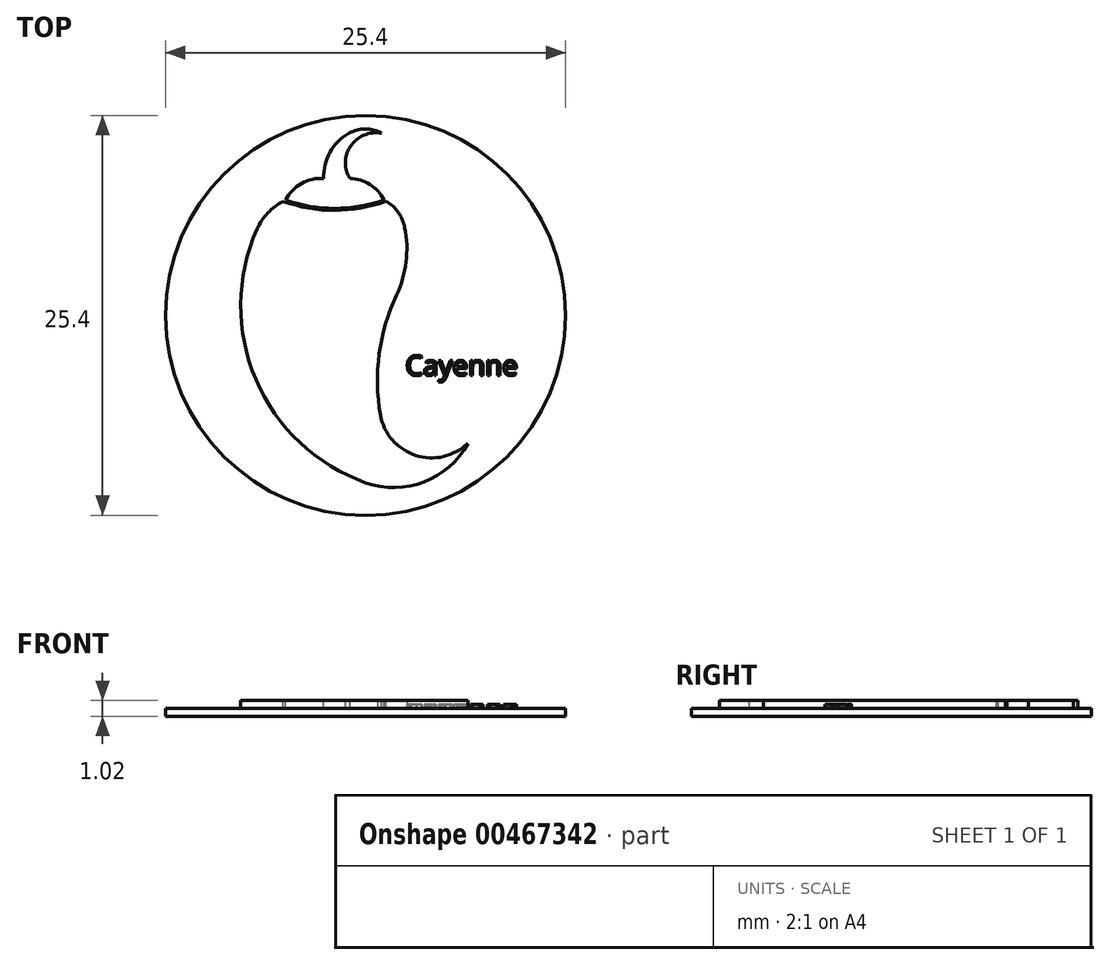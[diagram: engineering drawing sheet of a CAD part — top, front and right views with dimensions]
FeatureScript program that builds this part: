
annotation { "Feature Type Name" : "Feature", "Feature Type Description" : "" }
export const myFeature = defineFeature(function(context is Context, id is Id, definition is map)
    precondition{}
    {
        {
            var Q0;
            Q0=qCreatedBy(makeId("Top.planeOp"),FACE);
            var sketch = newSketch(context, id + "F0", { "sketchPlane" : qUnion([Q0])});
            skCircle(sketch, "E0", {"center": v(0, 0) * mm, "radius": 12.7 * mm});
            skSolve(sketch);
        }
        {
            var Q0;
            Q0 = qSketchRegion(id + "F0", true);
            extrude(context, id + "F1", {"entities" : qUnion([Q0]), "depth" : 0.5 * mm});
        }
        {
            var Q0;
            Q0=makeQuery(id+"F1.opExtrude","CAP_FACE",FACE,{"disambiguationData":[OSD([sQuery(id+"F0.wireOp",EDGE,"E0")])],"isStart":false});
            var sketch = newSketch(context, id + "F2", { "sketchPlane" : qUnion([Q0])});
            skArc(sketch, "E1", {"start": v(0, -10.63) * mm, "mid": v(3.71, -10.58) * mm, "end": v(6.5, -8.12) * mm});
            skArc(sketch, "E2", {"start": v(-6.9, 5.47) * mm, "mid": v(-6.96, -4.08) * mm, "end": v(0, -10.63) * mm});
            skArc(sketch, "E3", {"start": v(-4.06, 7.62) * mm, "mid": v(-5.75, 6.91) * mm, "end": v(-6.9, 5.47) * mm});
            skLineSegment(sketch, "E4", {"start": v(-4.06, 7.62) * mm, "end": v(0, 7.62) * mm});
            skArc(sketch, "E5", {"start": v(2.5, 5.58) * mm, "mid": v(1.6, 7.04) * mm, "end": v(0, 7.62) * mm});
            skArc(sketch, "E6", {"start": v(1.97, 1.3) * mm, "mid": v(2.57, 3.4) * mm, "end": v(2.5, 5.58) * mm});
            skArc(sketch, "E7", {"start": v(1.97, 1.3) * mm, "mid": v(0.87, -2.43) * mm, "end": v(0.95, -6.32) * mm});
            skArc(sketch, "E8", {"start": v(0.95, -6.32) * mm, "mid": v(3.18, -8.9) * mm, "end": v(6.5, -8.12) * mm});
            skSolve(sketch);
        }
        {
            var Q0;
            Q0 = qSketchRegion(id + "F2", true);
            extrude(context, id + "F3", {"entities" : qUnion([Q0]), "operationType" : NewBodyOperationType.ADD, "depth" : 0.5 * mm});
        }
        {
            var Q0;
            Q0=makeQuery(id+"F3.opExtrude","CAP_FACE",FACE,{"disambiguationData":[OSD([sQuery(id+"F2.wireOp",EDGE,"E1"),sQuery(id+"F2.wireOp",EDGE,"E2"),sQuery(id+"F2.wireOp",EDGE,"E3"),sQuery(id+"F2.wireOp",EDGE,"E4"),sQuery(id+"F2.wireOp",EDGE,"E5"),sQuery(id+"F2.wireOp",EDGE,"E6"),sQuery(id+"F2.wireOp",EDGE,"E7"),sQuery(id+"F2.wireOp",EDGE,"E8")])],"isStart":false});
            var sketch = newSketch(context, id + "F4", { "sketchPlane" : qUnion([Q0])});
            skArc(sketch, "E9", {"start": v(-2.65, 8.69) * mm, "mid": v(-4.07, 8.39) * mm, "end": v(-5.07, 7.32) * mm});
            skArc(sketch, "E10", {"start": v(-1.04, 11.57) * mm, "mid": v(-2.26, 10.36) * mm, "end": v(-2.65, 8.69) * mm});
            skArc(sketch, "E11", {"start": v(1.03, 11.57) * mm, "mid": v(0, 11.84) * mm, "end": v(-1.04, 11.57) * mm});
            skArc(sketch, "E12", {"start": v(1.03, 11.57) * mm, "mid": v(-0.1, 11.45) * mm, "end": v(-0.98, 10.7) * mm});
            skArc(sketch, "E13", {"start": v(-0.98, 10.7) * mm, "mid": v(-1.28, 9.7) * mm, "end": v(-0.98, 8.69) * mm});
            skArc(sketch, "E14", {"start": v(1.16, 7.34) * mm, "mid": v(0.28, 8.32) * mm, "end": v(-0.98, 8.69) * mm});
            skArc(sketch, "E15", {"start": v(-5.07, 7.32) * mm, "mid": v(-1.95, 7.04) * mm, "end": v(1.16, 7.34) * mm});
            skSolve(sketch);
        }
        {
            var Q0;
            Q0 = qSketchRegion(id + "F4", true);
            extrude(context, id + "F5", {"entities" : qUnion([Q0]), "operationType" : NewBodyOperationType.ADD, "oppositeDirection" : true, "depth" : 0.5 * mm});
        }
        {
            var Q0;
            Q0=makeQuery(id+"F5.boolean.opBoolean","MERGE",FACE,{"derivedFrom":[makeQuery(id+"F3.opExtrude","CAP_FACE",FACE,{"disambiguationData":[OSD([sQuery(id+"F2.wireOp",EDGE,"E1"),sQuery(id+"F2.wireOp",EDGE,"E2"),sQuery(id+"F2.wireOp",EDGE,"E3"),sQuery(id+"F2.wireOp",EDGE,"E4"),sQuery(id+"F2.wireOp",EDGE,"E5"),sQuery(id+"F2.wireOp",EDGE,"E6"),sQuery(id+"F2.wireOp",EDGE,"E7"),sQuery(id+"F2.wireOp",EDGE,"E8")])],"isStart":false}),makeQuery(id+"F5.opExtrude","CAP_FACE",FACE,{"disambiguationData":[OSD([sQuery(id+"F4.wireOp",EDGE,"E9"),sQuery(id+"F4.wireOp",EDGE,"E10"),sQuery(id+"F4.wireOp",EDGE,"E11"),sQuery(id+"F4.wireOp",EDGE,"E12"),sQuery(id+"F4.wireOp",EDGE,"E13"),sQuery(id+"F4.wireOp",EDGE,"E14"),sQuery(id+"F4.wireOp",EDGE,"E15")])],"isStart":true})]});
            var sketch = newSketch(context, id + "F6", { "sketchPlane" : qUnion([Q0])});
            skArc(sketch, "E16", {"start": v(-5.07, 7.32) * mm, "mid": v(-1.95, 6.8) * mm, "end": v(1.16, 7.34) * mm});
            skArc(sketch, "E17", {"start": v(-5.23, 7.25) * mm, "mid": v(-1.96, 6.67) * mm, "end": v(1.31, 7.26) * mm});
            skArc(sketch, "E18", {"start": v(-5.07, 7.32) * mm, "mid": v(-5.15, 7.29) * mm, "end": v(-5.23, 7.25) * mm});
            skArc(sketch, "E19", {"start": v(1.31, 7.26) * mm, "mid": v(1.24, 7.3) * mm, "end": v(1.16, 7.34) * mm});
            skSolve(sketch);
        }
        {
            var Q0;
            Q0 = qSketchRegion(id + "F6", true);
            extrude(context, id + "F7", {"entities" : qUnion([Q0]), "operationType" : NewBodyOperationType.REMOVE, "oppositeDirection" : true, "depth" : 0.5 * mm});
        }
        {
            var Q0;
            Q0=makeQuery(id+"F7.boolean.opBoolean","MERGE",FACE,{"derivedFrom":[makeQuery(id+"F1.opExtrude","CAP_FACE",FACE,{"disambiguationData":[OSD([sQuery(id+"F0.wireOp",EDGE,"E0")])],"isStart":false}),makeQuery(id+"F7.opExtrude","CAP_FACE",FACE,{"disambiguationData":[OSD([sQuery(id+"F6.wireOp",EDGE,"E16"),sQuery(id+"F6.wireOp",EDGE,"E17"),sQuery(id+"F6.wireOp",EDGE,"E18"),sQuery(id+"F6.wireOp",EDGE,"E19")])],"isStart":false})]});
            var sketch = newSketch(context, id + "F8", { "sketchPlane" : qUnion([Q0])});
            skText(sketch, "E20", { "text": "Cayenne", "fontName": "OpenSans-Regular.ttf"});
            const initialGuessF8  = {"E20": [0.00254, -0.00381, 1, 0, 0.00127]};
            skSetInitialGuess(sketch, initialGuessF8);
            skSolve(sketch);
        }
        {
            var Q0;
            Q0 = qSketchRegion(id + "F8", true);
            extrude(context, id + "F9", {"entities" : qUnion([Q0]), "operationType" : NewBodyOperationType.ADD, "depth" : 0.25 * mm});
        }
    });
